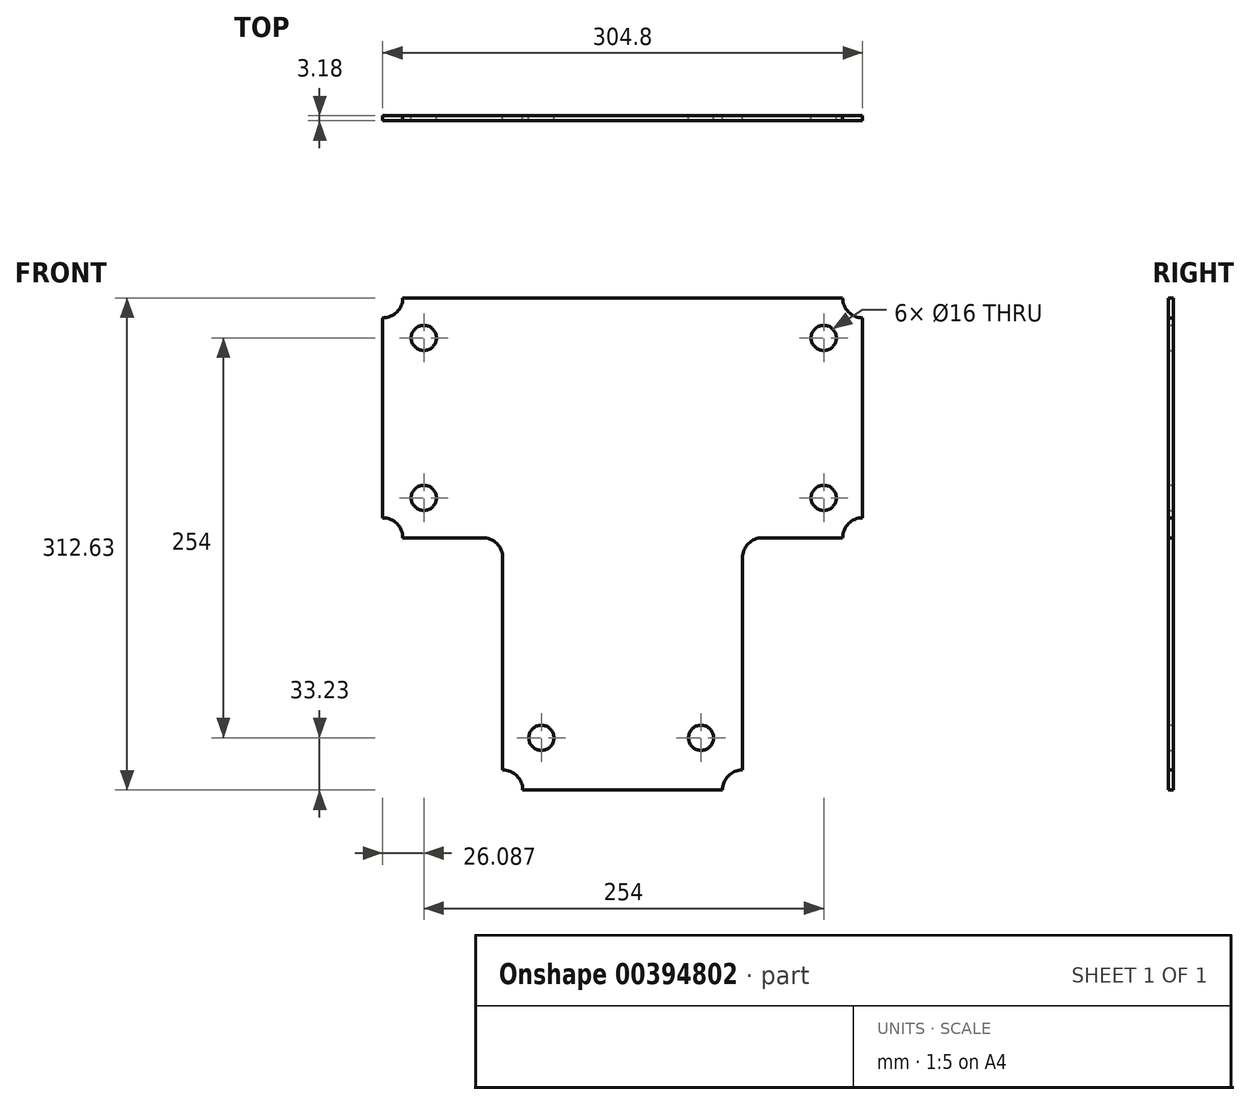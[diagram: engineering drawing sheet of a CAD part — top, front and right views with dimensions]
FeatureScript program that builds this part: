
annotation { "Feature Type Name" : "Feature", "Feature Type Description" : "" }
export const myFeature = defineFeature(function(context is Context, id is Id, definition is map)
    precondition{}
    {
        {
            var Q0;
            Q0=qCreatedBy(makeId("Front.planeOp"),FACE);
            var sketch = newSketch(context, id + "F0", { "sketchPlane" : qUnion([Q0])});
            skLineSegment(sketch, "E0.bottom", {"start": v(140.71, 76.2) * mm, "end": v(-138.69, 76.2) * mm});
            skLineSegment(sketch, "E0.top", {"start": v(140.71, -76.2) * mm, "end": v(89.78, -76.2) * mm});
            skLineSegment(sketch, "E0.left", {"start": v(153.41, 63.5) * mm, "end": v(153.41, -63.5) * mm});
            skLineSegment(sketch, "E0.right", {"start": v(-151.39, 63.5) * mm, "end": v(-151.39, -63.5) * mm});
            skPoint(sketch, "E0.middle", {"position": v(1.01, 0) * mm});
            skPoint(sketch, "E1", {"position": v(0, -76.2) * mm});
            skPoint(sketch, "E2", {"position": v(76.2, -76.2) * mm});
            skPoint(sketch, "E3", {"position": v(-76.2, -76.2) * mm});
            skLineSegment(sketch, "E4.top", {"start": v(64.38, -236.43) * mm, "end": v(-62.49, -236.43) * mm});
            skLineSegment(sketch, "E4.left", {"start": v(77.08, -88.9) * mm, "end": v(77.08, -223.73) * mm});
            skLineSegment(sketch, "E4.right", {"start": v(-75.19, -88.9) * mm, "end": v(-75.19, -223.73) * mm});
            skCircle(sketch, "E5", {"center": v(-125.3, -50.8) * mm, "radius": 8 * mm});
            skCircle(sketch, "E6", {"center": v(-125.3, 50.8) * mm, "radius": 8 * mm});
            skCircle(sketch, "E7", {"center": v(128.7, 50.8) * mm, "radius": 8 * mm});
            skCircle(sketch, "E8", {"center": v(128.7, -50.8) * mm, "radius": 8 * mm});
            skCircle(sketch, "E9", {"center": v(-50.67, -203.2) * mm, "radius": 8 * mm});
            skCircle(sketch, "E10", {"center": v(50.8, -203.2) * mm, "radius": 8 * mm});
            skArc(sketch, "E11", {"start": v(-151.39, 63.5) * mm, "mid": v(-142.4, 67.22) * mm, "end": v(-138.69, 76.2) * mm});
            skArc(sketch, "E12", {"start": v(-138.69, -76.2) * mm, "mid": v(-142.4, -67.22) * mm, "end": v(-151.39, -63.5) * mm});
            skArc(sketch, "E13", {"start": v(140.71, 76.2) * mm, "mid": v(144.43, 67.22) * mm, "end": v(153.41, 63.5) * mm});
            skArc(sketch, "E14", {"start": v(153.41, -63.5) * mm, "mid": v(144.43, -67.22) * mm, "end": v(140.71, -76.2) * mm});
            skArc(sketch, "E15", {"start": v(77.08, -223.73) * mm, "mid": v(68.1, -227.45) * mm, "end": v(64.38, -236.43) * mm});
            skArc(sketch, "E16", {"start": v(-62.49, -236.43) * mm, "mid": v(-66.2, -227.45) * mm, "end": v(-75.19, -223.73) * mm});
            skPoint(sketch, "E17", {"position": v(-75.19, -223.73) * mm});
            skPoint(sketch, "E18", {"position": v(-62.49, -236.43) * mm});
            skArc(sketch, "E19.filletArc", {"start": v(89.78, -76.2) * mm, "mid": v(80.8, -79.92) * mm, "end": v(77.08, -88.9) * mm});
            skLineSegment(sketch, "E20", {"start": v(-138.69, -76.2) * mm, "end": v(-87.89, -76.2) * mm});
            skArc(sketch, "E21.filletArc", {"start": v(-75.19, -88.9) * mm, "mid": v(-78.9, -79.92) * mm, "end": v(-87.89, -76.2) * mm});
            skSolve(sketch);
        }
        {
            var Q0;
            Q0=makeQuery(id+"F0.imprint","IMPRINT",FACE,{"disambiguationData":[TD([[makeQuery(id+"F0.imprint","IMPRINT",EDGE,{"derivedFrom":sQuery(id+"F0.wireOp",EDGE,"E0.bottom")}),1.0]])]});
            var Q1;
            Q1=makeQuery(id+"F0.imprint","IMPRINT",FACE,{"disambiguationData":[TD([[makeQuery(id+"F0.imprint","IMPRINT",EDGE,{"derivedFrom":sQuery(id+"F0.wireOp",EDGE,"E4.top")}),-1.0]])]});
            extrude(context, id + "F1", {"entities" : qUnion([Q0, Q1]), "depth" : 3.17 * mm});
        }
    });
